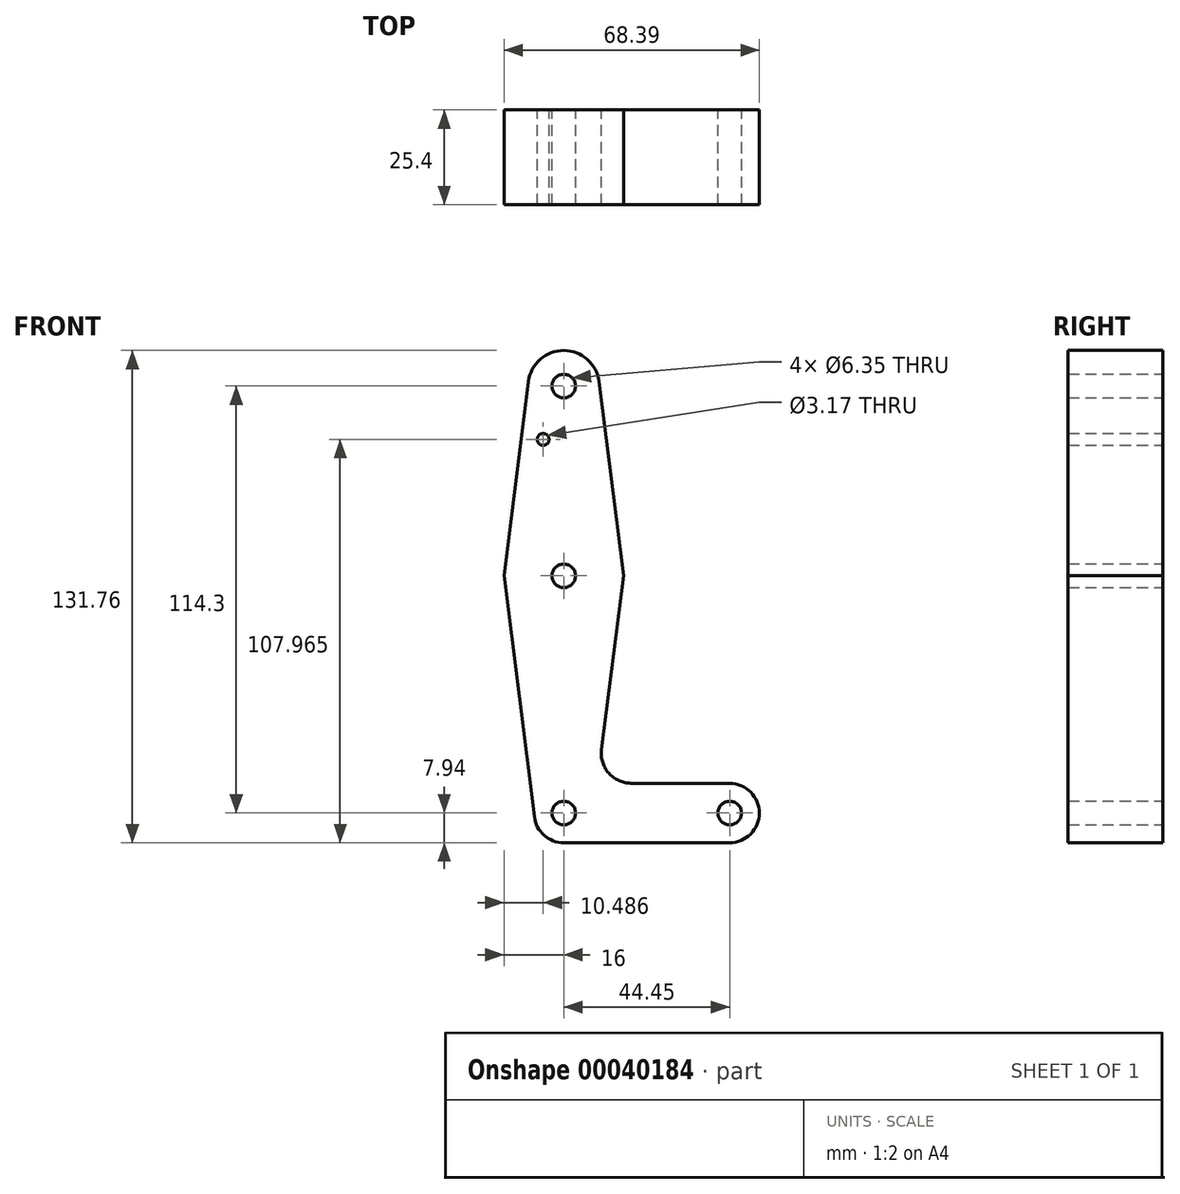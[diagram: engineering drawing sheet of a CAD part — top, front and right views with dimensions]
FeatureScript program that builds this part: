
annotation { "Feature Type Name" : "Feature", "Feature Type Description" : "" }
export const myFeature = defineFeature(function(context is Context, id is Id, definition is map)
    precondition{}
    {
        {
            var Q0;
            Q0=qCreatedBy(makeId("Front.planeOp"),FACE);
            var sketch = newSketch(context, id + "F0", { "sketchPlane" : qUnion([Q0])});
            skLineSegment(sketch, "E0", {"start": v(0, 0) * mm, "end": v(0, 50.8) * mm, "construction": true});
            skLineSegment(sketch, "E1", {"start": v(0, 50.8) * mm, "end": v(0, -63.5) * mm, "construction": true});
            skLineSegment(sketch, "E2", {"start": v(0, -63.5) * mm, "end": v(44.45, -63.5) * mm, "construction": true});
            skLineSegment(sketch, "E3", {"start": v(44.45, -63.5) * mm, "end": v(0, -63.5) * mm, "construction": true});
            skCircle(sketch, "E4", {"center": v(0, 50.8) * mm, "radius": 9.53 * mm});
            skCircle(sketch, "E5", {"center": v(0, 0) * mm, "radius": 15.88 * mm});
            skCircle(sketch, "E6", {"center": v(0, -63.5) * mm, "radius": 7.94 * mm});
            skCircle(sketch, "E7", {"center": v(44.45, -63.5) * mm, "radius": 7.94 * mm});
            skLineSegment(sketch, "E8", {"start": v(-9.45, 52) * mm, "end": v(-16, 0) * mm});
            skLineSegment(sketch, "E9", {"start": v(9.45, 52) * mm, "end": v(16, 0) * mm});
            skLineSegment(sketch, "E10", {"start": v(-16, 0) * mm, "end": v(-7.88, -64.5) * mm});
            skLineSegment(sketch, "E11", {"start": v(10.13, -46.57) * mm, "end": v(16, 0) * mm});
            skLineSegment(sketch, "E12", {"start": v(18, -55.51) * mm, "end": v(44.46, -55.56) * mm});
            skLineSegment(sketch, "E13", {"start": v(0, -71.44) * mm, "end": v(44.45, -71.44) * mm});
            skCircle(sketch, "E14", {"center": v(0, 50.8) * mm, "radius": 3.18 * mm});
            skCircle(sketch, "E15", {"center": v(-5.51, 36.53) * mm, "radius": 1.59 * mm});
            skCircle(sketch, "E16", {"center": v(0, 0) * mm, "radius": 3.18 * mm});
            skCircle(sketch, "E17", {"center": v(0, -63.5) * mm, "radius": 3.18 * mm});
            skCircle(sketch, "E18", {"center": v(44.45, -63.5) * mm, "radius": 3.18 * mm});
            skArc(sketch, "E19.filletArc", {"start": v(10.13, -46.57) * mm, "mid": v(12.05, -52.82) * mm, "end": v(18, -55.51) * mm});
            skSolve(sketch);
        }
        {
            var Q0;
            Q0=makeQuery(id+"F0.imprint","IMPRINT",FACE,{"disambiguationData":[TD([[makeQuery(id+"F0.imprint","IMPRINT",EDGE,{"derivedFrom":sQuery(id+"F0.wireOp",EDGE,"E14")}),-1.0]])]});
            extrude(context, id + "F1", {"entities" : qUnion([Q0]), "depth" : 3.05 * mm});
        }
        {
            var Q0;
            Q0 = qSketchRegion(id + "F0", true);
            extrude(context, id + "F2", {"entities" : qUnion([Q0]), "operationType" : NewBodyOperationType.ADD, "depth" : 25.4 * mm});
        }
    });
